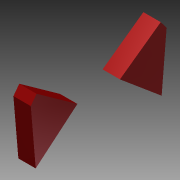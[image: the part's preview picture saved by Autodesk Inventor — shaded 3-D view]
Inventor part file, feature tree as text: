
AUTODESK INVENTOR PART (.ipt)
format: ipt  version: 2014 (Build 180170000, 170)  size: 778,240 bytes
history: native  units: in
note: dims shown in document units (in); Inventor stores cm internally (conversion verified against a paired STEP export)
features: sketch x22, extrude x15, plane x9, projected_geometry x6, loft x4, other x3, mirror x1, emboss x1
ambient origin geometry x8: Origin, YZ Plane, XZ Plane, XY Plane, X Axis, Y Axis, Z Axis, Center Point
bodies: Solid1 (feature_tree)
feature tree (61):
  sketch  "Sketch1"  dims[d0=0.7559in d1=0.7559in]
  plane  "Work Plane1"
  loft  "Loft1"
  extrude  "Extrusion1"  Depth=0.2in
  plane  "Work Plane4"
  loft  "Loft2"
  plane  "Work Plane5"
  loft  "Loft3"
  loft  "Loft4"
  extrude  "Extrusion2"  TaperAngle=0.0deg  [1 undecoded]
  plane  "Work Plane6"
  extrude  "Extrusion3"  Depth=1.0in
  extrude  "Extrusion4"  Depth=1.0651in
  extrude  "Extrusion5"  Depth=0.962in
  plane  "Work Plane7"
  extrude  "Extrusion6"  Depth=0.075in
  plane  "Work Plane8"
  other  "Work Axis1"
  plane  "Work Plane9"
  extrude  "Extrusion7"  Depth=0.06in
  mirror  "Mirror3"
  extrude  "Extrusion8"  Depth=0.1in
  plane  "Work Plane10"
  extrude  "Extrusion9"  Depth=0.0625in
  plane  "Work Plane11"
  extrude  "Extrusion10"  Depth=0.075in
  extrude  "Extrusion11"  TaperAngle=0.0deg  [1 undecoded]
  extrude  "Extrusion12"  Depth=0.2in
  extrude  "Extrusion13"  TaperAngle=0.0deg  [1 undecoded]
  emboss  "Emboss1"
  extrude  "Extrusion15"  Depth=0.01in
  extrude  "Extrusion16"  Depth=0.0344in
  sketch  "Sketch2"  dims[d2=0.9963in d3=0.2in]
  sketch  "Sketch3"  dims[d4=0.5in d6=0.08in]
  sketch  "Sketch4"  dims[d7=0.55in d8=150.0deg]
  other  "Edges1"
  sketch  "Sketch5"  dims[d9=150.0deg d14=0.33in]
  projected_geometry  "Projected Loop1"
  other  "Edges2"
  sketch  "Sketch6"  dims[d15=0.66in d18=0.0in d19=90.0deg]
  sketch  "Sketch7"  dims[d20=0.0in d21=90.0deg d22=1.0in]
  sketch  "Sketch8"  dims[d26=1.0651in d28=1.0651in]
  sketch  "Sketch9"  dims[d29=0.0in d30=0.962in]
  sketch  "Sketch10"  dims[d31=0.962in d32=0.075in]
  sketch  "Sketch11"  dims[d33=0.15in d34=0.06in]
  sketch  "Sketch12"  dims[d35=0.1in d36=0.05in]
  sketch  "Sketch13"  dims[d37=0.45in d38=0.0in d39=0.0625in]
  projected_geometry  "Projected Loop2"
  projected_geometry  "Projected Loop3"
  sketch  "Sketch14"  dims[d40=0.01in d41=0.075in]
  projected_geometry  "Projected Loop4"
  sketch  "Sketch15"  dims[d42=0.01in d43=0.0in d44=90.0deg]
  sketch  "Sketch16"  dims[d45=0.0in d46=90.0deg d47=0.2in]
  sketch  "Sketch17"  dims[d48=0.07in d49=0.0in d50=90.0deg]
  sketch  "Sketch18"  dims[d51=0.0in d52=90.0deg d53=0.01in]
  sketch  "Sketch19"  dims[d54=0.01in d55=0.0344in]
  sketch  "Sketch20"  dims[d56=150.0deg]
  sketch  "Sketch22"  dims[d57=60.0deg]
  projected_geometry  "Projected Loop5"
  sketch  "Sketch23"  dims[d58=150.0deg d59=0.7in d60=0.05in d61=0.05in d62=0.05in d63=0.05in d64=0.05in d65=0.01in d66=0.0in d67=90.0deg d68=0.0in d69=90.0deg d70=0.1in d71=0.4in d72=0.15in d73=0.05in d74=0.0in d75=0.02in d77=0.15in d78=0.02in d79=0.1in d80=0.1in d81=0.1in d82=0.02in d83=0.15in d84=0.05in d85=0.0in d86=0.045in d87=0.0in d88=0.025in d89=0.0in d90=0.02in d91=0.02in d92=0.005in d93=0.0in d94=90.0deg d95=0.4466in d96=1.0in d97=0.0in d98=1.0in d99=0.0in d100=0.6528in d101=0.0in d102=0.0in d103=1.0in d104=0.0in d106=90.0deg d107=1.0in d108=0.0in d109=1.65in d110=0.1in d111=0.075in d112=0.0in d113=0.1in d114=0.075in d115=0.0in d116=0.05in d117=0.0in d121=0.05in d122=0.0in d123=0.1in d124=0.0in]
  projected_geometry  "Projected Loop6"
note: 3 required parameter values undecoded (feature->parameter linkage not recoverable at this tier; creation-order binding heuristic only, values carry confidence <= 0.55)
